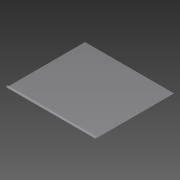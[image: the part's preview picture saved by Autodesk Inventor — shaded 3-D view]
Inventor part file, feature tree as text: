
AUTODESK INVENTOR PART (.ipt)
format: ipt  version: 2013 (Build 170138000, 138)  size: 100,352 bytes
history: native  units: in
note: dims shown in document units (in); Inventor stores cm internally (conversion verified against a paired STEP export)
features: sheet_metal_op x7, sketch x3, other x3
ambient origin geometry x8: Origin, YZ Plane, XZ Plane, XY Plane, X Axis, Y Axis, Z Axis, Center Point
bodies: Solid1 (feature_tree)
feature tree (13):
  sheet_metal_op  "Face1"
  sheet_metal_op  "Flange1"
  sheet_metal_op  "Flange2"
  sketch  "Sketch1"  dims[d0=54.0in]
  other  "Plate1"
  sketch  "Sketch2"  dims[d1=48.0in]
  other  "Plate2"
  sheet_metal_op  "Bend1"
  sheet_metal_op  "Corner1"
  sketch  "Sketch3"  dims[d2=0.2125in d3=0.2125in d4=0.1063in d5=0.425in d6=0.2125in d7=1.0in d8=90.0deg d9=0.2125in d10=0.85in d11=0.2125in d12=0.2125in d13=0.2125in d14=0.1063in d15=0.425in d16=0.2125in d17=1.0in d18=90.0deg d19=0.2125in d20=0.85in d21=0.2125in d22=0.2125in]
  other  "Plate3"
  sheet_metal_op  "Bend2"
  sheet_metal_op  "Corner2"
